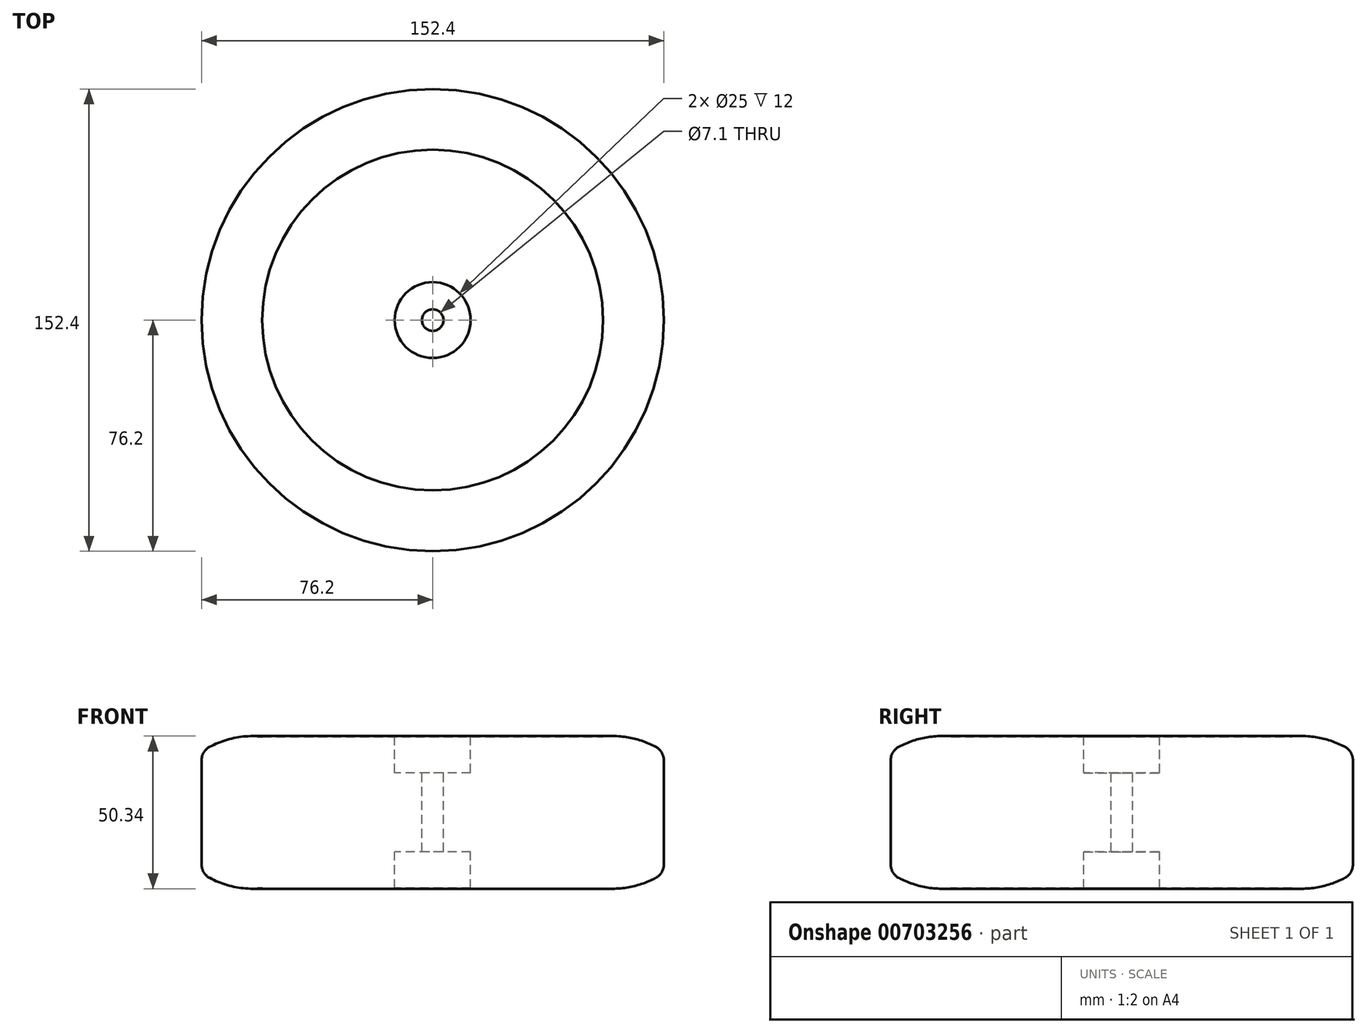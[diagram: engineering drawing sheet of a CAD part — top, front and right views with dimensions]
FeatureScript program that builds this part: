
annotation { "Feature Type Name" : "Feature", "Feature Type Description" : "" }
export const myFeature = defineFeature(function(context is Context, id is Id, definition is map)
    precondition{}
    {
        {
            var Q0;
            Q0=qCreatedBy(makeId("Right.planeOp"),FACE);
            var sketch = newSketch(context, id + "F0", { "sketchPlane" : qUnion([Q0])});
            skLineSegment(sketch, "E0", {"start": v(0, 0) * mm, "end": v(0, 50) * mm});
            skLineSegment(sketch, "E1", {"start": v(0, 50) * mm, "end": v(-56.2, 50) * mm});
            skLineSegment(sketch, "E2", {"start": v(0, 0) * mm, "end": v(-56.2, 0) * mm});
            skLineSegment(sketch, "E3", {"start": v(-76.2, 45) * mm, "end": v(-76.2, 5) * mm});
            skArc(sketch, "E4", {"start": v(-56.2, 50) * mm, "mid": v(-66.64, 49.27) * mm, "end": v(-76.2, 45) * mm});
            skArc(sketch, "E5", {"start": v(-76.2, 5) * mm, "mid": v(-66.64, 0.73) * mm, "end": v(-56.2, 0) * mm});
            skSolve(sketch);
        }
        {
            var Q0;
            Q0=makeQuery(id+"F0.imprint","IMPRINT",FACE,{"disambiguationData":[TD([[makeQuery(id+"F0.imprint","IMPRINT",EDGE,{"derivedFrom":sQuery(id+"F0.wireOp",EDGE,"E0")}),1.0]])]});
            var Q1;
            Q1=sQuery(id+"F0.wireOp",EDGE,"E0");
            revolve(context, id + "F1", {"surfaceOperationType" : NewSurfaceOperationType.NEW, "entities" : qUnion([Q0]), "axis" : qUnion([Q1]), "revolveType" : RevolveType.FULL});
        }
        {
            var Q0;
            Q0=makeQuery(id+"F1.opRevolve","SWEPT_FACE",FACE,{"disambiguationData":[OSD([sQuery(id+"F0.wireOp",EDGE,"E1")])]});
            var sketch = newSketch(context, id + "F2", { "sketchPlane" : qUnion([Q0])});
            skCircle(sketch, "E6.0", {"center": v(0, 0) * mm, "radius": 56.2 * mm});
            skCircle(sketch, "E7", {"center": v(0, 0) * mm, "radius": 12.5 * mm});
            skCircle(sketch, "E8", {"center": v(0, 0) * mm, "radius": 3.55 * mm});
            skCircle(sketch, "E9.cCircle", {"center": v(0, 0) * mm, "radius": 6 * mm, "construction": true});
            skLineSegment(sketch, "E9.0", {"start": v(-3.46, 6) * mm, "end": v(3.46, 6) * mm});
            skLineSegment(sketch, "E9.1", {"start": v(3.46, 6) * mm, "end": v(6.93, 0) * mm});
            skLineSegment(sketch, "E9.2", {"start": v(6.93, 0) * mm, "end": v(3.46, -6) * mm});
            skLineSegment(sketch, "E9.3", {"start": v(3.46, -6) * mm, "end": v(-3.46, -6) * mm});
            skLineSegment(sketch, "E9.4", {"start": v(-3.46, -6) * mm, "end": v(-6.93, 0) * mm});
            skLineSegment(sketch, "E9.5", {"start": v(-6.93, 0) * mm, "end": v(-3.46, 6) * mm});
            skPoint(sketch, "E9.0.midPoint", {"position": v(0, 6) * mm});
            skSolve(sketch);
        }
        {
            var Q0;
            Q0=makeQuery(id+"F2.imprint","IMPRINT",FACE,{"disambiguationData":[TD([[makeQuery(id+"F2.imprint","IMPRINT",EDGE,{"derivedFrom":sQuery(id+"F2.wireOp",EDGE,"E8")}),1.0]])]});
            extrude(context, id + "F3", {"entities" : qUnion([Q0]), "operationType" : NewBodyOperationType.REMOVE, "endBound" : BoundingType.THROUGH_ALL, "oppositeDirection" : true, "depth" : 25 * mm, "offsetDistance" : 25 * mm});
        }
        {
            var Q0;
            Q0=makeQuery(id+"F2.imprint","IMPRINT",FACE,{"disambiguationData":[TD([[makeQuery(id+"F2.imprint","IMPRINT",EDGE,{"derivedFrom":sQuery(id+"F2.wireOp",EDGE,"E7")}),1.0]])]});
            var Q1;
            Q1=makeQuery(id+"F2.imprint","IMPRINT",FACE,{"disambiguationData":[TD([[makeQuery(id+"F2.imprint","IMPRINT",EDGE,{"derivedFrom":sQuery(id+"F2.wireOp",EDGE,"E8")}),-1.0]])]});
            extrude(context, id + "F4", {"entities" : qUnion([Q0, Q1]), "operationType" : NewBodyOperationType.REMOVE, "oppositeDirection" : true, "depth" : 12 * mm, "offsetDistance" : 25 * mm});
        }
        {
            var Q0;
            Q0=makeQuery(id+"F2.imprint","IMPRINT",FACE,{"disambiguationData":[TD([[makeQuery(id+"F2.imprint","IMPRINT",EDGE,{"derivedFrom":sQuery(id+"F2.wireOp",EDGE,"E7")}),1.0]])]});
            var Q1;
            Q1=makeQuery(id+"F2.imprint","IMPRINT",FACE,{"disambiguationData":[TD([[makeQuery(id+"F2.imprint","IMPRINT",EDGE,{"derivedFrom":sQuery(id+"F2.wireOp",EDGE,"E8")}),-1.0]])]});
            extrude(context, id + "F5", {"entities" : qUnion([Q0, Q1]), "operationType" : NewBodyOperationType.REMOVE, "oppositeDirection" : true, "depth" : 50 * mm, "offsetDistance" : 25 * mm, "hasSecondDirection" : true, "secondDirectionOppositeDirection" : true, "secondDirectionDepth" : 38 * mm});
        }
        {
            var Q0;
            Q0=makeQuery(id+"F1.opRevolve","SWEPT_EDGE",EDGE,{"disambiguationData":[OSD([sQuery(id+"F0.wireOp",EDGE,"E3"),sQuery(id+"F0.wireOp",EDGE,"E4")])]});
            var Q1;
            Q1=makeQuery(id+"F1.opRevolve","SWEPT_EDGE",EDGE,{"disambiguationData":[OSD([sQuery(id+"F0.wireOp",EDGE,"E3"),sQuery(id+"F0.wireOp",EDGE,"E5")])]});
            fillet(context, id + "F6", {"entities" : qUnion([Q0, Q1]), "radius" : 5 * mm, "tangentPropagation" : true, "allowEdgeOverflow" : false});
        }
    });
